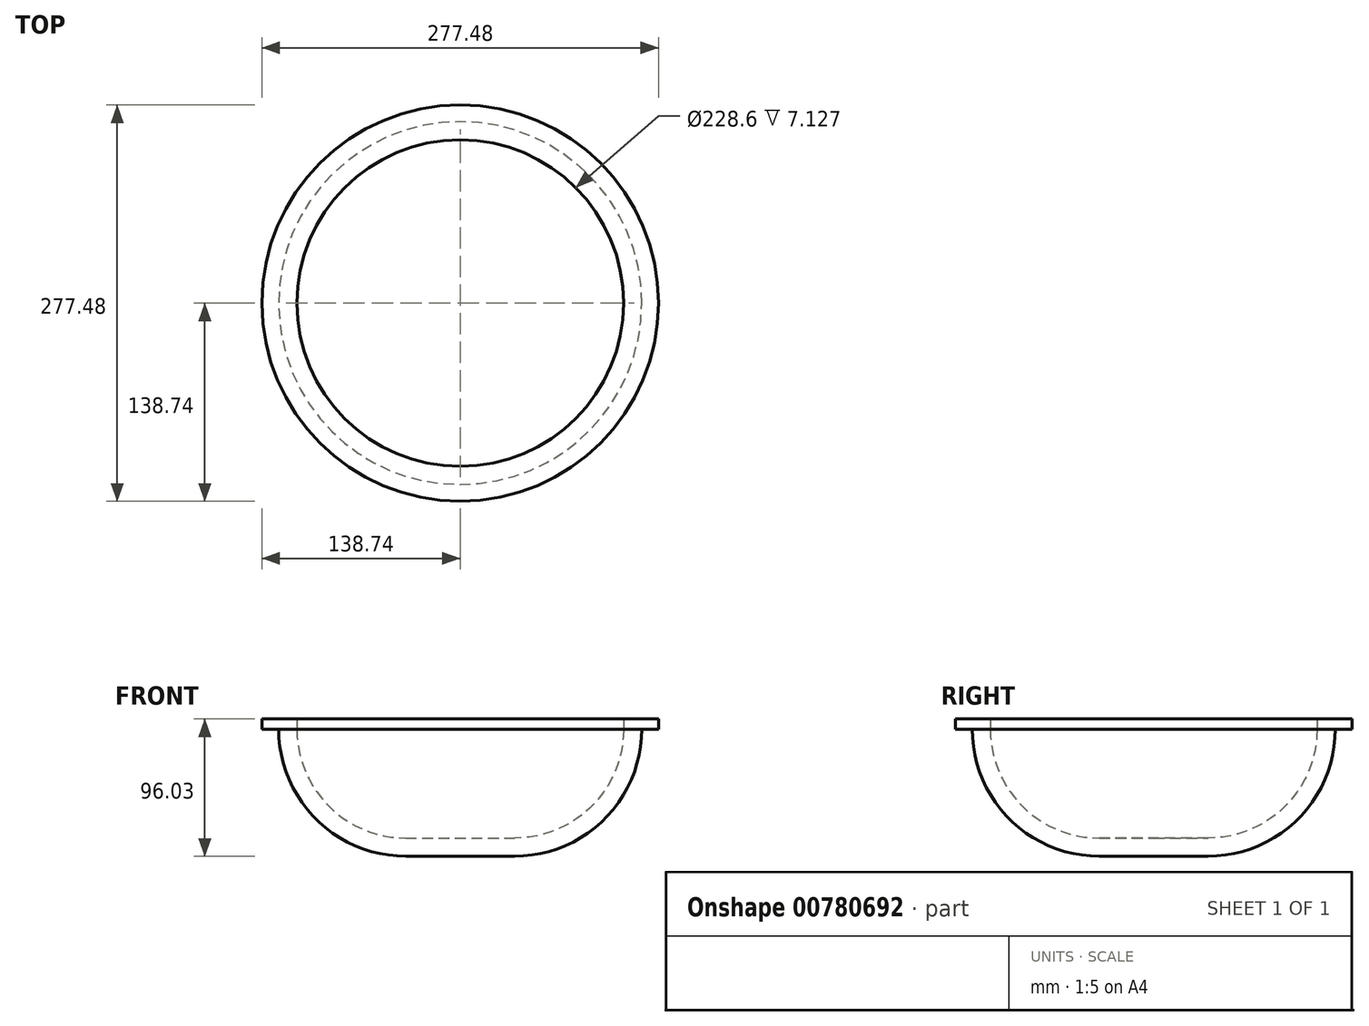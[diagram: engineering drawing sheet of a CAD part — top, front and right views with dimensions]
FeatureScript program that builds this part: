
annotation { "Feature Type Name" : "Feature", "Feature Type Description" : "" }
export const myFeature = defineFeature(function(context is Context, id is Id, definition is map)
    precondition{}
    {
        {
            var Q0;
            Q0=qCreatedBy(makeId("Right.planeOp"),FACE);
            var sketch = newSketch(context, id + "F0", { "sketchPlane" : qUnion([Q0])});
            skLineSegment(sketch, "E0.bottom", {"start": v(-57.41, -9.12) * mm, "end": v(-19.31, -9.12) * mm});
            skLineSegment(sketch, "E0.top", {"start": v(-57.41, -21.82) * mm, "end": v(-19.31, -21.82) * mm});
            skLineSegment(sketch, "E0.left", {"start": v(-57.41, -9.12) * mm, "end": v(-57.41, -21.82) * mm});
            skLineSegment(sketch, "E0.right", {"start": v(-19.31, -9.12) * mm, "end": v(-19.31, -21.82) * mm, "construction": true});
            skLineSegment(sketch, "E1.bottom", {"start": v(56.89, 74.2) * mm, "end": v(81.33, 74.2) * mm});
            skLineSegment(sketch, "E1.top", {"start": v(69.59, 67.08) * mm, "end": v(81.33, 67.08) * mm});
            skLineSegment(sketch, "E1.left", {"start": v(56.89, 74.2) * mm, "end": v(56.89, 67.08) * mm});
            skLineSegment(sketch, "E1.right", {"start": v(81.33, 74.2) * mm, "end": v(81.33, 67.08) * mm});
            skArc(sketch, "E2", {"start": v(-19.31, -21.82) * mm, "mid": v(43.55, 4.22) * mm, "end": v(69.59, 67.08) * mm});
            skArc(sketch, "E3", {"start": v(-19.31, -9.12) * mm, "mid": v(34.57, 13.2) * mm, "end": v(56.89, 67.08) * mm});
            skLineSegment(sketch, "E4", {"start": v(-57.41, -21.82) * mm, "end": v(-57.41, 97) * mm, "construction": true});
            skSolve(sketch);
        }
        {
            var Q0;
            Q0=makeQuery(id+"F0.imprint","IMPRINT",FACE,{"disambiguationData":[TD([[makeQuery(id+"F0.imprint","IMPRINT",EDGE,{"derivedFrom":sQuery(id+"F0.wireOp",EDGE,"E0.bottom")}),-1.0]])]});
            var Q1;
            Q1=sQuery(id+"F0.wireOp",EDGE,"E4");
            revolve(context, id + "F1", {"surfaceOperationType" : NewSurfaceOperationType.NEW, "entities" : qUnion([Q0]), "axis" : qUnion([Q1]), "revolveType" : RevolveType.FULL});
        }
    });
